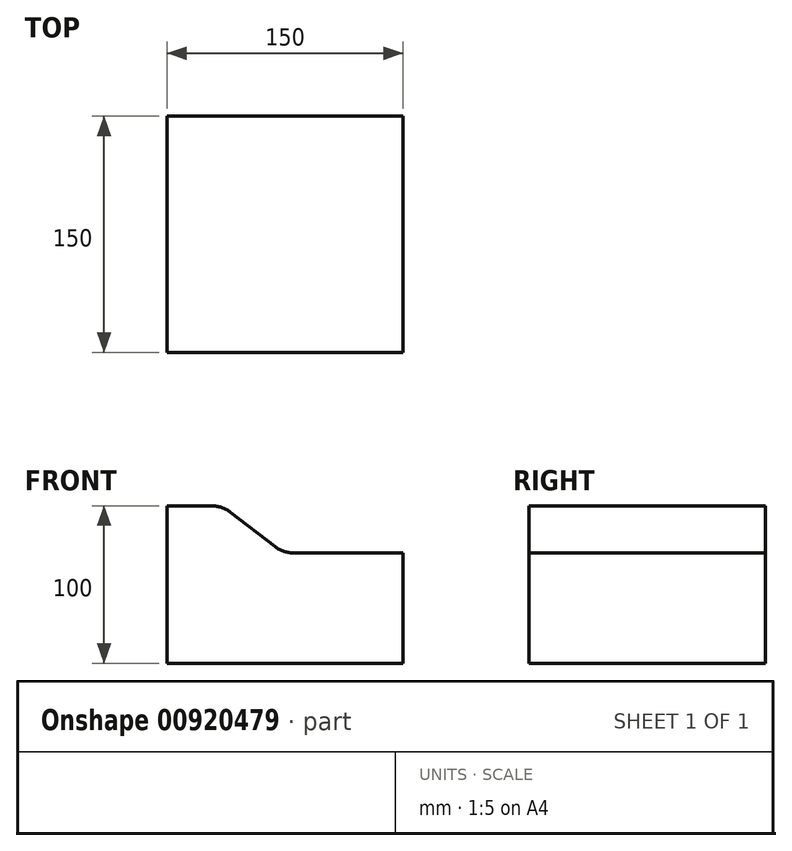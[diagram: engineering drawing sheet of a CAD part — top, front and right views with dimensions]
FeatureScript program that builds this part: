
annotation { "Feature Type Name" : "Feature", "Feature Type Description" : "" }
export const myFeature = defineFeature(function(context is Context, id is Id, definition is map)
    precondition{}
    {
        {
            var Q0;
            Q0=qCreatedBy(makeId("Front.planeOp"),FACE);
            var sketch = newSketch(context, id + "F0", { "sketchPlane" : qUnion([Q0])});
            skLineSegment(sketch, "E0.bottom", {"start": v(0, 0) * mm, "end": v(28.2, 0) * mm});
            skLineSegment(sketch, "E0.top", {"start": v(0, -100) * mm, "end": v(150, -100) * mm});
            skLineSegment(sketch, "E0.left", {"start": v(0, 0) * mm, "end": v(0, -100) * mm});
            skLineSegment(sketch, "E0.right", {"start": v(150, -30) * mm, "end": v(150, -100) * mm});
            skLineSegment(sketch, "E1", {"start": v(80.8, -30) * mm, "end": v(150, -30) * mm});
            skLineSegment(sketch, "E2", {"start": v(68.6, -25.85) * mm, "end": v(40.4, -4.15) * mm});
            skPoint(sketch, "E3.visualSharp", {"position": v(35, 0) * mm});
            skArc(sketch, "E3.filletArc", {"start": v(40.4, -4.15) * mm, "mid": v(34.64, -1.07) * mm, "end": v(28.2, 0) * mm});
            skPoint(sketch, "E4.visualSharp", {"position": v(74, -30) * mm});
            skArc(sketch, "E4.filletArc", {"start": v(68.6, -25.85) * mm, "mid": v(74.36, -28.93) * mm, "end": v(80.8, -30) * mm});
            skPoint(sketch, "E5.visualSharp", {"position": v(150, -30) * mm});
            skLineSegment(sketch, "E5.filletArc", {"start": v(150, -30) * mm, "end": v(150, -30) * mm});
            skPoint(sketch, "E6.visualSharp", {"position": v(0, 0) * mm});
            skLineSegment(sketch, "E6.filletArc", {"start": v(0, 0) * mm, "end": v(0, 0) * mm});
            skSolve(sketch);
        }
        {
            var Q0;
            Q0=makeQuery(id+"F0.imprint","IMPRINT",FACE,{"disambiguationData":[TD([[makeQuery(id+"F0.imprint","IMPRINT",EDGE,{"derivedFrom":sQuery(id+"F0.wireOp",EDGE,"E0.bottom")}),-1.0]])]});
            extrude(context, id + "F1", {"entities" : qUnion([Q0]), "depth" : 150 * mm, "offsetDistance" : 25 * mm});
        }
    });
